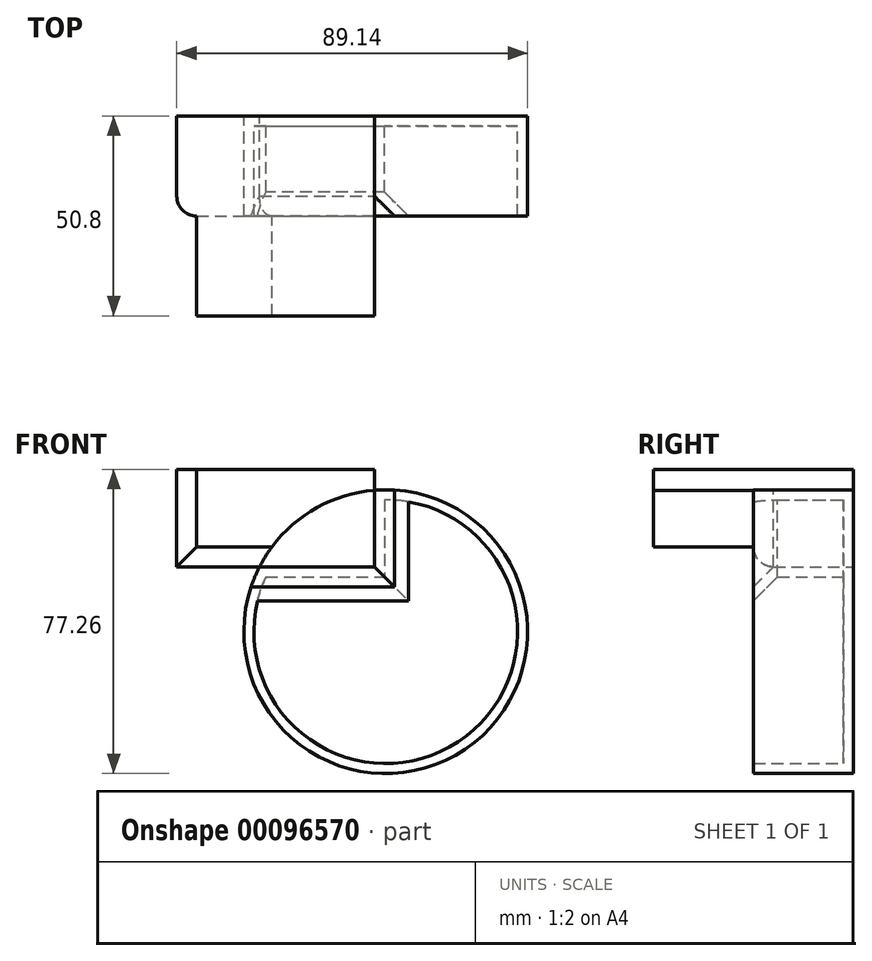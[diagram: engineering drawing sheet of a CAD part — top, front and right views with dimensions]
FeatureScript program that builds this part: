
annotation { "Feature Type Name" : "Feature", "Feature Type Description" : "" }
export const myFeature = defineFeature(function(context is Context, id is Id, definition is map)
    precondition{}
    {
        {
            var Q0;
            Q0=qCreatedBy(makeId("Front.planeOp"),FACE);
            var sketch = newSketch(context, id + "F0", { "sketchPlane" : qUnion([Q0])});
            skCircle(sketch, "E0", {"center": v(0, 0) * mm, "radius": 36.04 * mm});
            skLineSegment(sketch, "E1.bottom", {"start": v(-53.1, 41.22) * mm, "end": v(-2.9, 41.22) * mm});
            skLineSegment(sketch, "E1.top", {"start": v(-53.1, 16.49) * mm, "end": v(-2.9, 16.49) * mm});
            skLineSegment(sketch, "E1.left", {"start": v(-53.1, 41.22) * mm, "end": v(-53.1, 16.49) * mm});
            skLineSegment(sketch, "E1.right", {"start": v(-2.9, 41.22) * mm, "end": v(-2.9, 16.49) * mm});
            skSolve(sketch);
        }
        {
            var Q0;
            {var subQ4=sQuery(id+"F0.wireOp",EDGE,"E1.bottom");Q0=makeQuery(id+"F0.imprint","IMPRINT",FACE,{"disambiguationData":[TD([[makeQuery(id+"F0.imprint","IMPRINT",EDGE,{"derivedFrom":subQ4}),-1.0]])]});}
            var Q1;
            {var subQ0=sQuery(id+"F0.wireOp",EDGE,"E1.top");var subQ1=sQuery(id+"F0.wireOp",EDGE,"E0");var subQ2=makeQuery(id+"F0.imprint","INTERSECT",VERTEX,{"derivedFrom":[subQ1,subQ0]});Q1=makeQuery(id+"F0.imprint","IMPRINT",FACE,{"disambiguationData":[TD([[makeQuery(id+"F0.imprint","IMPRINT",EDGE,{"disambiguationData":[TD([[subQ2,-1.0]])],"derivedFrom":subQ1}),1.0]])]});}
            extrude(context, id + "F1", {"entities" : qUnion([Q0, Q1]), "depth" : 25.4 * mm});
        }
        {
            var Q0;
            Q0=makeQuery(id+"F1.opExtrude","CAP_EDGE",EDGE,{"disambiguationData":[OSD([sQuery(id+"F0.wireOp",EDGE,"E1.left")])],"isStart":false});
            var Q1;
            {var subQ0=sQuery(id+"F0.wireOp",EDGE,"E1.top");Q1=makeQuery(id+"F1.opExtrude","CAP_EDGE",EDGE,{"disambiguationData":[OSD([subQ0]),TDD([makeQuery(id+"F0.imprint","IMPRINT",EDGE,{"disambiguationData":[TD([[makeQuery(id+"F0.imprint","INTERSECT",VERTEX,{"derivedFrom":[subQ0,sQuery(id+"F0.wireOp",EDGE,"E1.left")]}),-1.0]])],"derivedFrom":subQ0})])],"isStart":false});}
            fillet(context, id + "F2", {"entities" : qUnion([Q0, Q1]), "radius" : 5.08 * mm, "tangentPropagation" : true, "allowEdgeOverflow" : false});
        }
        {
            var Q0;
            {var subQ0=sQuery(id+"F0.wireOp",EDGE,"E1.top");Q0=makeQuery(id+"F1.opExtrude","CAP_EDGE",EDGE,{"disambiguationData":[OSD([subQ0]),TDD([makeQuery(id+"F0.imprint","IMPRINT",EDGE,{"disambiguationData":[TD([[makeQuery(id+"F0.imprint","INTERSECT",VERTEX,{"derivedFrom":[subQ0,sQuery(id+"F0.wireOp",EDGE,"E1.right")]}),1.0]])],"derivedFrom":subQ0})])],"isStart":false});}
            var Q1;
            {var subQ0=sQuery(id+"F0.wireOp",EDGE,"E1.right");Q1=makeQuery(id+"F1.opExtrude","CAP_EDGE",EDGE,{"disambiguationData":[OSD([subQ0]),TDD([makeQuery(id+"F0.imprint","IMPRINT",EDGE,{"disambiguationData":[TD([[makeQuery(id+"F0.imprint","INTERSECT",VERTEX,{"derivedFrom":[sQuery(id+"F0.wireOp",EDGE,"E1.top"),subQ0]}),1.0]])],"derivedFrom":subQ0})])],"isStart":false});}
            chamfer(context, id + "F3", {"entities" : qUnion([Q0, Q1]), "width" : 5.08 * mm, "tangentPropagation" : true});
        }
        {
            var Q0;
            Q0=makeQuery(id+"F1.opExtrude","CAP_FACE",FACE,{"disambiguationData":[OSD([sQuery(id+"F0.wireOp",EDGE,"E0"),sQuery(id+"F0.wireOp",EDGE,"E1.top"),sQuery(id+"F0.wireOp",EDGE,"E1.right")])],"isStart":false});
            shell(context, id + "F4", {"entities" : qUnion([Q0]), "thickness" : 2.54 * mm});
        }
        {
            var Q0;
            Q0=makeQuery(id+"F1.opExtrude","CAP_FACE",FACE,{"disambiguationData":[OSD([sQuery(id+"F0.wireOp",EDGE,"E0"),sQuery(id+"F0.wireOp",EDGE,"E1.bottom"),sQuery(id+"F0.wireOp",EDGE,"E1.top"),sQuery(id+"F0.wireOp",EDGE,"E1.left"),sQuery(id+"F0.wireOp",EDGE,"E1.right")])],"isStart":false});
            extrude(context, id + "F5", {"entities" : qUnion([Q0]), "operationType" : NewBodyOperationType.ADD, "depth" : 25.4 * mm});
        }
    });
